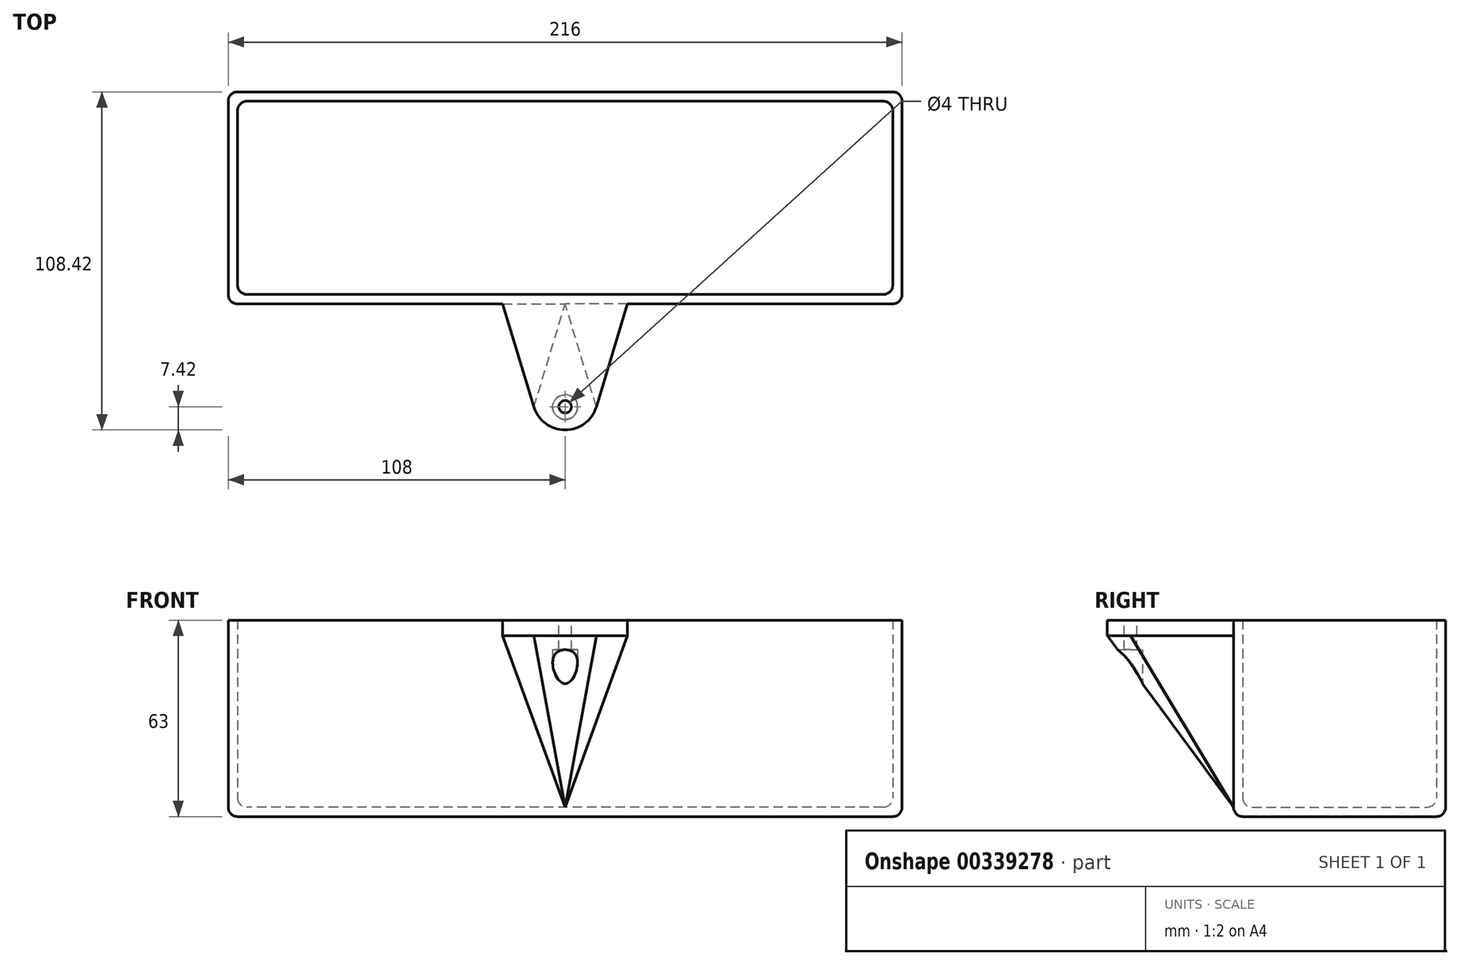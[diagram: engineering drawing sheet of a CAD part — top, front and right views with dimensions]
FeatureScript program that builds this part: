
annotation { "Feature Type Name" : "Feature", "Feature Type Description" : "" }
export const myFeature = defineFeature(function(context is Context, id is Id, definition is map)
    precondition{}
    {
        {
            var Q0;
            Q0=qCreatedBy(makeId("Top.planeOp"),FACE);
            var sketch = newSketch(context, id + "F0", { "sketchPlane" : qUnion([Q0])});
            skLineSegment(sketch, "E0.bottom", {"start": v(105, -31) * mm, "end": v(-105, -31) * mm});
            skLineSegment(sketch, "E0.top", {"start": v(105, 31) * mm, "end": v(-105, 31) * mm});
            skLineSegment(sketch, "E0.left", {"start": v(105, -31) * mm, "end": v(105, 31) * mm});
            skLineSegment(sketch, "E0.right", {"start": v(-105, -31) * mm, "end": v(-105, 31) * mm});
            skPoint(sketch, "E0.middle", {"position": v(0, 0) * mm});
            skLineSegment(sketch, "E1.0", {"start": v(108, -34) * mm, "end": v(-108, -34) * mm});
            skLineSegment(sketch, "E1.1", {"start": v(108, -34) * mm, "end": v(108, 34) * mm});
            skLineSegment(sketch, "E1.2", {"start": v(108, 34) * mm, "end": v(-108, 34) * mm});
            skLineSegment(sketch, "E1.3", {"start": v(-108, -34) * mm, "end": v(-108, 34) * mm});
            skSolve(sketch);
        }
        {
            var Q0;
            Q0=makeQuery(id+"F0.imprint","IMPRINT",FACE,{"disambiguationData":[TD([[makeQuery(id+"F0.imprint","IMPRINT",EDGE,{"derivedFrom":sQuery(id+"F0.wireOp",EDGE,"E0.bottom")}),-1.0]])]});
            var Q1;
            Q1=makeQuery(id+"F0.imprint","IMPRINT",FACE,{"disambiguationData":[TD([[makeQuery(id+"F0.imprint","IMPRINT",EDGE,{"derivedFrom":sQuery(id+"F0.wireOp",EDGE,"E0.bottom")}),1.0]])]});
            extrude(context, id + "F1", {"entities" : qUnion([Q0, Q1]), "depth" : 3 * mm});
        }
        {
            var Q0;
            Q0=makeQuery(id+"F1.opExtrude","CAP_FACE",FACE,{"disambiguationData":[OSD([sQuery(id+"F0.wireOp",EDGE,"E1.0"),sQuery(id+"F0.wireOp",EDGE,"E1.1"),sQuery(id+"F0.wireOp",EDGE,"E1.2"),sQuery(id+"F0.wireOp",EDGE,"E1.3")])],"isStart":false});
            var sketch = newSketch(context, id + "F2", { "sketchPlane" : qUnion([Q0])});
            skLineSegment(sketch, "E2.0", {"start": v(105, 31) * mm, "end": v(-105, 31) * mm});
            skLineSegment(sketch, "E3.0", {"start": v(-105, -31) * mm, "end": v(-105, 31) * mm});
            skLineSegment(sketch, "E4.0", {"start": v(105, -31) * mm, "end": v(-105, -31) * mm});
            skLineSegment(sketch, "E5.0", {"start": v(105, -31) * mm, "end": v(105, 31) * mm});
            skLineSegment(sketch, "E6.0", {"start": v(108, 34) * mm, "end": v(-108, 34) * mm});
            skLineSegment(sketch, "E7.0", {"start": v(-108, -34) * mm, "end": v(-108, 34) * mm});
            skLineSegment(sketch, "E8.0", {"start": v(108, -34) * mm, "end": v(-108, -34) * mm});
            skLineSegment(sketch, "E9.0", {"start": v(108, -34) * mm, "end": v(108, 34) * mm});
            skSolve(sketch);
        }
        {
            var Q0;
            Q0 = qSketchRegion(id + "F2", true);
            extrude(context, id + "F3", {"entities" : qUnion([Q0]), "operationType" : NewBodyOperationType.ADD, "depth" : 60 * mm});
        }
        {
            var Q0;
            Q0=makeQuery(id+"F3.boolean.opBoolean","MERGE",EDGE,{"derivedFrom":[makeQuery(id+"F1.opExtrude","SWEPT_EDGE",EDGE,{"disambiguationData":[OSD([sQuery(id+"F0.wireOp",EDGE,"E1.0"),sQuery(id+"F0.wireOp",EDGE,"E1.3")])]}),makeQuery(id+"F3.opExtrude","SWEPT_EDGE",EDGE,{"disambiguationData":[OSD([sQuery(id+"F2.wireOp",EDGE,"E7.0"),sQuery(id+"F2.wireOp",EDGE,"E8.0")])]})]});
            var Q1;
            Q1=makeQuery(id+"F3.opExtrude","SWEPT_EDGE",EDGE,{"disambiguationData":[OSD([sQuery(id+"F2.wireOp",EDGE,"E2.0"),sQuery(id+"F2.wireOp",EDGE,"E3.0")])]});
            var Q2;
            Q2=makeQuery(id+"F3.opExtrude","SWEPT_EDGE",EDGE,{"disambiguationData":[OSD([sQuery(id+"F2.wireOp",EDGE,"E3.0"),sQuery(id+"F2.wireOp",EDGE,"E4.0")])]});
            var Q3;
            Q3=makeQuery(id+"F3.boolean.opBoolean","MERGE",EDGE,{"derivedFrom":[makeQuery(id+"F1.opExtrude","SWEPT_EDGE",EDGE,{"disambiguationData":[OSD([sQuery(id+"F0.wireOp",EDGE,"E1.0"),sQuery(id+"F0.wireOp",EDGE,"E1.1")])]}),makeQuery(id+"F3.opExtrude","SWEPT_EDGE",EDGE,{"disambiguationData":[OSD([sQuery(id+"F2.wireOp",EDGE,"E8.0"),sQuery(id+"F2.wireOp",EDGE,"E9.0")])]})]});
            var Q4;
            Q4=makeQuery(id+"F3.opExtrude","SWEPT_EDGE",EDGE,{"disambiguationData":[OSD([sQuery(id+"F2.wireOp",EDGE,"E5.0"),sQuery(id+"F2.wireOp",EDGE,"E4.0")])]});
            var Q5;
            Q5=makeQuery(id+"F3.opExtrude","SWEPT_EDGE",EDGE,{"disambiguationData":[OSD([sQuery(id+"F2.wireOp",EDGE,"E2.0"),sQuery(id+"F2.wireOp",EDGE,"E5.0")])]});
            var Q6;
            Q6=makeQuery(id+"F3.boolean.opBoolean","MERGE",EDGE,{"derivedFrom":[makeQuery(id+"F1.opExtrude","SWEPT_EDGE",EDGE,{"disambiguationData":[OSD([sQuery(id+"F0.wireOp",EDGE,"E1.1"),sQuery(id+"F0.wireOp",EDGE,"E1.2")])]}),makeQuery(id+"F3.opExtrude","SWEPT_EDGE",EDGE,{"disambiguationData":[OSD([sQuery(id+"F2.wireOp",EDGE,"E6.0"),sQuery(id+"F2.wireOp",EDGE,"E9.0")])]})]});
            var Q7;
            Q7=makeQuery(id+"F3.boolean.opBoolean","MERGE",EDGE,{"derivedFrom":[makeQuery(id+"F1.opExtrude","SWEPT_EDGE",EDGE,{"disambiguationData":[OSD([sQuery(id+"F0.wireOp",EDGE,"E1.2"),sQuery(id+"F0.wireOp",EDGE,"E1.3")])]}),makeQuery(id+"F3.opExtrude","SWEPT_EDGE",EDGE,{"disambiguationData":[OSD([sQuery(id+"F2.wireOp",EDGE,"E6.0"),sQuery(id+"F2.wireOp",EDGE,"E7.0")])]})]});
            fillet(context, id + "F4", {"entities" : qUnion([Q0, Q1, Q2, Q3, Q4, Q5, Q6, Q7]), "radius" : 3 * mm, "tangentPropagation" : true, "allowEdgeOverflow" : false});
        }
        {
            var Q0;
            Q0=makeQuery(id+"F1.opExtrude","CAP_FACE",FACE,{"disambiguationData":[OSD([sQuery(id+"F0.wireOp",EDGE,"E1.0"),sQuery(id+"F0.wireOp",EDGE,"E1.1"),sQuery(id+"F0.wireOp",EDGE,"E1.2"),sQuery(id+"F0.wireOp",EDGE,"E1.3")])],"isStart":true});
            fillet(context, id + "F5", {"entities" : qUnion([Q0]), "radius" : 3 * mm, "tangentPropagation" : true, "allowEdgeOverflow" : false});
        }
        {
            var Q0;
            Q0=makeQuery(id+"F3.opExtrude","CAP_FACE",FACE,{"disambiguationData":[OSD([sQuery(id+"F2.wireOp",EDGE,"E2.0"),sQuery(id+"F2.wireOp",EDGE,"E3.0"),sQuery(id+"F2.wireOp",EDGE,"E5.0"),sQuery(id+"F2.wireOp",EDGE,"E6.0"),sQuery(id+"F2.wireOp",EDGE,"E7.0"),sQuery(id+"F2.wireOp",EDGE,"E4.0"),sQuery(id+"F2.wireOp",EDGE,"E8.0"),sQuery(id+"F2.wireOp",EDGE,"E9.0")])],"isStart":false});
            var sketch = newSketch(context, id + "F6", { "sketchPlane" : qUnion([Q0])});
            skLineSegment(sketch, "E10.0", {"start": v(102, -31) * mm, "end": v(-102, -31) * mm});
            skPoint(sketch, "E11.endSnap0", {"position": v(0, -34) * mm});
            skLineSegment(sketch, "E12", {"start": v(0, -34) * mm, "end": v(-20, -34) * mm});
            skLineSegment(sketch, "E13", {"start": v(0, -34) * mm, "end": v(20, -34) * mm});
            skLineSegment(sketch, "E14", {"start": v(10, -67) * mm, "end": v(20, -34) * mm});
            skLineSegment(sketch, "E15", {"start": v(-10, -67) * mm, "end": v(-20, -34) * mm});
            skArc(sketch, "E16", {"start": v(-10, -67) * mm, "mid": v(0, -74.42) * mm, "end": v(10, -67) * mm});
            skSolve(sketch);
        }
        {
            var Q0;
            Q0=makeQuery(id+"F1.opExtrude","CAP_FACE",FACE,{"disambiguationData":[OSD([sQuery(id+"F0.wireOp",EDGE,"E1.0"),sQuery(id+"F0.wireOp",EDGE,"E1.1"),sQuery(id+"F0.wireOp",EDGE,"E1.2"),sQuery(id+"F0.wireOp",EDGE,"E1.3")])],"isStart":false});
            fillet(context, id + "F7", {"entities" : qUnion([Q0]), "radius" : 3 * mm, "tangentPropagation" : true, "allowEdgeOverflow" : false});
        }
        {
            var Q0;
            Q0=makeQuery(id+"F6.imprint","IMPRINT",FACE,{"disambiguationData":[TD([[makeQuery(id+"F6.imprint","IMPRINT",EDGE,{"derivedFrom":sQuery(id+"F6.wireOp",EDGE,"E12")}),1.0]])]});
            extrude(context, id + "F8", {"entities" : qUnion([Q0]), "operationType" : NewBodyOperationType.ADD, "oppositeDirection" : true, "depth" : 5 * mm});
        }
        {
            var Q0;
            {var subQ0=sQuery(id+"F0.wireOp",EDGE,"E1.0");Q0=makeQuery(id+"F5.opFillet","BLEND_EDGE",EDGE,{"blendedFrom":[makeQuery(id+"F1.opExtrude","CAP_EDGE",EDGE,{"disambiguationData":[OSD([subQ0])],"isStart":true}),makeQuery(id+"F3.boolean.opBoolean","MERGE",FACE,{"derivedFrom":[makeQuery(id+"F1.opExtrude","SWEPT_FACE",FACE,{"disambiguationData":[OSD([subQ0])]}),makeQuery(id+"F3.opExtrude","SWEPT_FACE",FACE,{"disambiguationData":[OSD([sQuery(id+"F2.wireOp",EDGE,"E8.0")])]})]})],"blendedInto":[makeQuery(id+"F3.boolean.opBoolean","MERGE",FACE,{"derivedFrom":[makeQuery(id+"F1.opExtrude","SWEPT_FACE",FACE,{"disambiguationData":[OSD([subQ0])]}),makeQuery(id+"F3.opExtrude","SWEPT_FACE",FACE,{"disambiguationData":[OSD([sQuery(id+"F2.wireOp",EDGE,"E8.0")])]})]})]});}
            cPoint(context, id + "F9", {"entities" : qUnion([Q0]), "parameter" : 0.5});
        }
        {
            var Q1;
            Q1=makeQuery(id+"F8.opExtrude","CAP_FACE",FACE,{"disambiguationData":[OSD([sQuery(id+"F6.wireOp",EDGE,"E12"),sQuery(id+"F6.wireOp",EDGE,"E13"),sQuery(id+"F6.wireOp",EDGE,"E14"),sQuery(id+"F6.wireOp",EDGE,"E15"),sQuery(id+"F6.wireOp",EDGE,"E16")])],"isStart":false});
            var Q2;
            Q2 = qCreatedBy(id + "F9" ,VERTEX);
            loft(context, id + "F10", {"operationType" : NewBodyOperationType.ADD, "sheetProfilesArray" : [{ "sheetProfileEntities" : qUnion([Q1]) }, { "sheetProfileEntities" : qUnion([Q2]) }]});
        }
        {
            var Q0;
            Q0=makeQuery(id+"F8.boolean.opBoolean","MERGE",FACE,{"derivedFrom":[makeQuery(id+"F3.opExtrude","CAP_FACE",FACE,{"disambiguationData":[OSD([sQuery(id+"F2.wireOp",EDGE,"E2.0"),sQuery(id+"F2.wireOp",EDGE,"E3.0"),sQuery(id+"F2.wireOp",EDGE,"E5.0"),sQuery(id+"F2.wireOp",EDGE,"E6.0"),sQuery(id+"F2.wireOp",EDGE,"E7.0"),sQuery(id+"F2.wireOp",EDGE,"E4.0"),sQuery(id+"F2.wireOp",EDGE,"E8.0"),sQuery(id+"F2.wireOp",EDGE,"E9.0")])],"isStart":false}),makeQuery(id+"F8.opExtrude","CAP_FACE",FACE,{"disambiguationData":[OSD([sQuery(id+"F6.wireOp",EDGE,"E12"),sQuery(id+"F6.wireOp",EDGE,"E13"),sQuery(id+"F6.wireOp",EDGE,"E14"),sQuery(id+"F6.wireOp",EDGE,"E15"),sQuery(id+"F6.wireOp",EDGE,"E16")])],"isStart":true})]});
            var sketch = newSketch(context, id + "F11", { "sketchPlane" : qUnion([Q0])});
            skLineSegment(sketch, "E17", {"start": v(10, -67) * mm, "end": v(-10, -67) * mm});
            skCircle(sketch, "E18", {"center": v(0, -67) * mm, "radius": 2 * mm});
            skSolve(sketch);
        }
        {
            var Q0;
            {var subQ0=sQuery(id+"F11.wireOp",EDGE,"E18");var subQ1=sQuery(id+"F11.wireOp",EDGE,"E17");var subQ2=makeQuery(id+"F11.imprint","INTERSECT",VERTEX,{"disambiguationData":[OD(0.0)],"derivedFrom":[subQ1,subQ0]});Q0=makeQuery(id+"F11.imprint","IMPRINT",FACE,{"disambiguationData":[TD([[makeQuery(id+"F11.imprint","IMPRINT",EDGE,{"disambiguationData":[TD([[subQ2,-1.0]])],"derivedFrom":subQ1}),1.0]])]});}
            var Q1;
            {var subQ0=sQuery(id+"F11.wireOp",EDGE,"E18");var subQ1=sQuery(id+"F11.wireOp",EDGE,"E17");var subQ2=makeQuery(id+"F11.imprint","INTERSECT",VERTEX,{"disambiguationData":[OD(0.0)],"derivedFrom":[subQ1,subQ0]});Q1=makeQuery(id+"F11.imprint","IMPRINT",FACE,{"disambiguationData":[TD([[makeQuery(id+"F11.imprint","IMPRINT",EDGE,{"disambiguationData":[TD([[subQ2,-1.0]])],"derivedFrom":subQ1}),-1.0]])]});}
            extrude(context, id + "F12", {"entities" : qUnion([Q0, Q1]), "operationType" : NewBodyOperationType.REMOVE, "oppositeDirection" : true, "depth" : 25 * mm});
        }
        {
            var Q0;
            Q0=makeQuery(id+"F1.opExtrude","CAP_FACE",FACE,{"disambiguationData":[OSD([sQuery(id+"F0.wireOp",EDGE,"E1.0"),sQuery(id+"F0.wireOp",EDGE,"E1.1"),sQuery(id+"F0.wireOp",EDGE,"E1.2"),sQuery(id+"F0.wireOp",EDGE,"E1.3")])],"isStart":true});
            var sketch = newSketch(context, id + "F13", { "sketchPlane" : qUnion([Q0])});
            skCircle(sketch, "E19", {"center": v(0, 67.12) * mm, "radius": 4 * mm});
            skSolve(sketch);
        }
        {
            var Q0;
            Q0=makeQuery(id+"F13.imprint","IMPRINT",FACE,{"disambiguationData":[TD([[makeQuery(id+"F13.imprint","IMPRINT",EDGE,{"derivedFrom":sQuery(id+"F13.wireOp",EDGE,"E19")}),1.0]])]});
            extrude(context, id + "F14", {"entities" : qUnion([Q0]), "operationType" : NewBodyOperationType.REMOVE, "oppositeDirection" : true, "depth" : 53.5 * mm});
        }
    });
